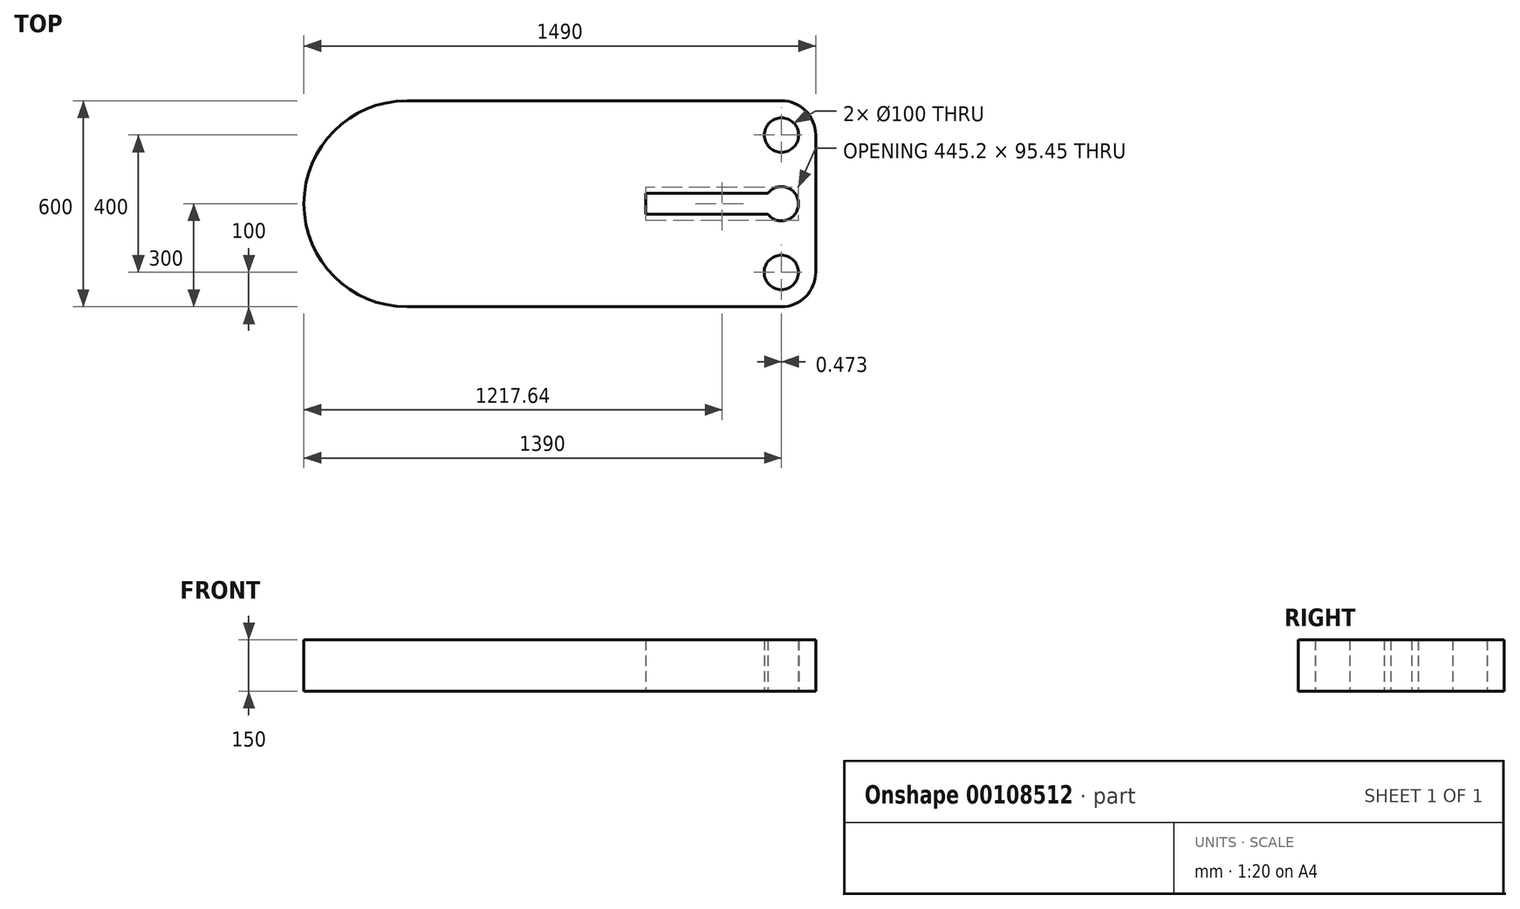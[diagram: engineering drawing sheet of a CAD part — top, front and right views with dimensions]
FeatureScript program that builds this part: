
annotation { "Feature Type Name" : "Feature", "Feature Type Description" : "" }
export const myFeature = defineFeature(function(context is Context, id is Id, definition is map)
    precondition{}
    {
        {
            var Q0;
            Q0=qCreatedBy(makeId("Top.planeOp"),FACE);
            var sketch = newSketch(context, id + "F0", { "sketchPlane" : qUnion([Q0])});
            skLineSegment(sketch, "E0.bottom", {"start": v(495, -300) * mm, "end": v(-595, -300) * mm});
            skLineSegment(sketch, "E0.top", {"start": v(495, 300) * mm, "end": v(-595, 300) * mm});
            skLineSegment(sketch, "E0.left", {"start": v(595, -200) * mm, "end": v(595, 200) * mm});
            skLineSegment(sketch, "E0.right", {"start": v(-595, -300) * mm, "end": v(-595, 300) * mm});
            skPoint(sketch, "E0.middle", {"position": v(0, 0) * mm});
            skArc(sketch, "E1", {"start": v(-595, 300) * mm, "mid": v(-895, 0) * mm, "end": v(-595, -300) * mm});
            skCircle(sketch, "E2", {"center": v(495, -200) * mm, "radius": 50 * mm});
            skCircle(sketch, "E3", {"center": v(495.47, 200) * mm, "radius": 50 * mm});
            skPoint(sketch, "E4.visualSharp", {"position": v(595, -300) * mm});
            skArc(sketch, "E4.filletArc", {"start": v(495, -300) * mm, "mid": v(565.71, -270.71) * mm, "end": v(595, -200) * mm});
            skPoint(sketch, "E5.visualSharp", {"position": v(595, 300) * mm});
            skArc(sketch, "E5.filletArc", {"start": v(595, 200) * mm, "mid": v(565.71, 270.71) * mm, "end": v(495, 300) * mm});
            skArc(sketch, "E6", {"start": v(455.24, -30) * mm, "mid": v(545.24, 0) * mm, "end": v(455.24, 30) * mm});
            skLineSegment(sketch, "E7", {"start": v(100.04, 0) * mm, "end": v(125.14, 0) * mm, "construction": true});
            skLineSegment(sketch, "E8.bottom", {"start": v(455.24, -30) * mm, "end": v(100.04, -30) * mm});
            skLineSegment(sketch, "E8.top", {"start": v(455.24, 30) * mm, "end": v(100.04, 30) * mm});
            skLineSegment(sketch, "E8.right", {"start": v(100.04, -30) * mm, "end": v(100.04, 30) * mm});
            skPoint(sketch, "E8.middle", {"position": v(310.2, 0) * mm});
            skLineSegment(sketch, "E9.trimOffspring", {"start": v(495.06, -150) * mm, "end": v(495, -200) * mm, "construction": true});
            skPoint(sketch, "E10.orphan", {"position": v(520.34, -30) * mm});
            skPoint(sketch, "E11.orphan", {"position": v(520.34, 30) * mm});
            skSolve(sketch);
        }
        {
            var Q0;
            Q0=makeQuery(id+"F0.imprint","IMPRINT",FACE,{"disambiguationData":[TD([[makeQuery(id+"F0.imprint","IMPRINT",EDGE,{"derivedFrom":sQuery(id+"F0.wireOp",EDGE,"E0.right")}),1.0]])]});
            var Q1;
            Q1=makeQuery(id+"F0.imprint","IMPRINT",FACE,{"disambiguationData":[TD([[makeQuery(id+"F0.imprint","IMPRINT",EDGE,{"derivedFrom":sQuery(id+"F0.wireOp",EDGE,"E0.bottom")}),-1.0]])]});
            extrude(context, id + "F1", {"entities" : qUnion([Q0, Q1]), "depth" : 150 * mm});
        }
    });
